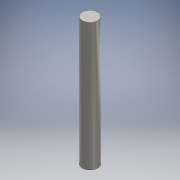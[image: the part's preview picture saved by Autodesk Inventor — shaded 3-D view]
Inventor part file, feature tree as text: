
AUTODESK INVENTOR PART (.ipt)
format: ipt  version: 2016 (Build 200138000, 138)  size: 89,088 bytes
history: native  units: mm
features: other x1, extrude x1, sketch x1
ambient origin geometry x8: Origin, YZ Plane, XZ Plane, XY Plane, X Axis, Y Axis, Z Axis, Center Point
bodies: Body1 (feature_tree)
feature tree (3):
  other  "ソリッド1"
  extrude  "押し出し1"  Depth=1.2mm
  sketch  "スケッチ1"
